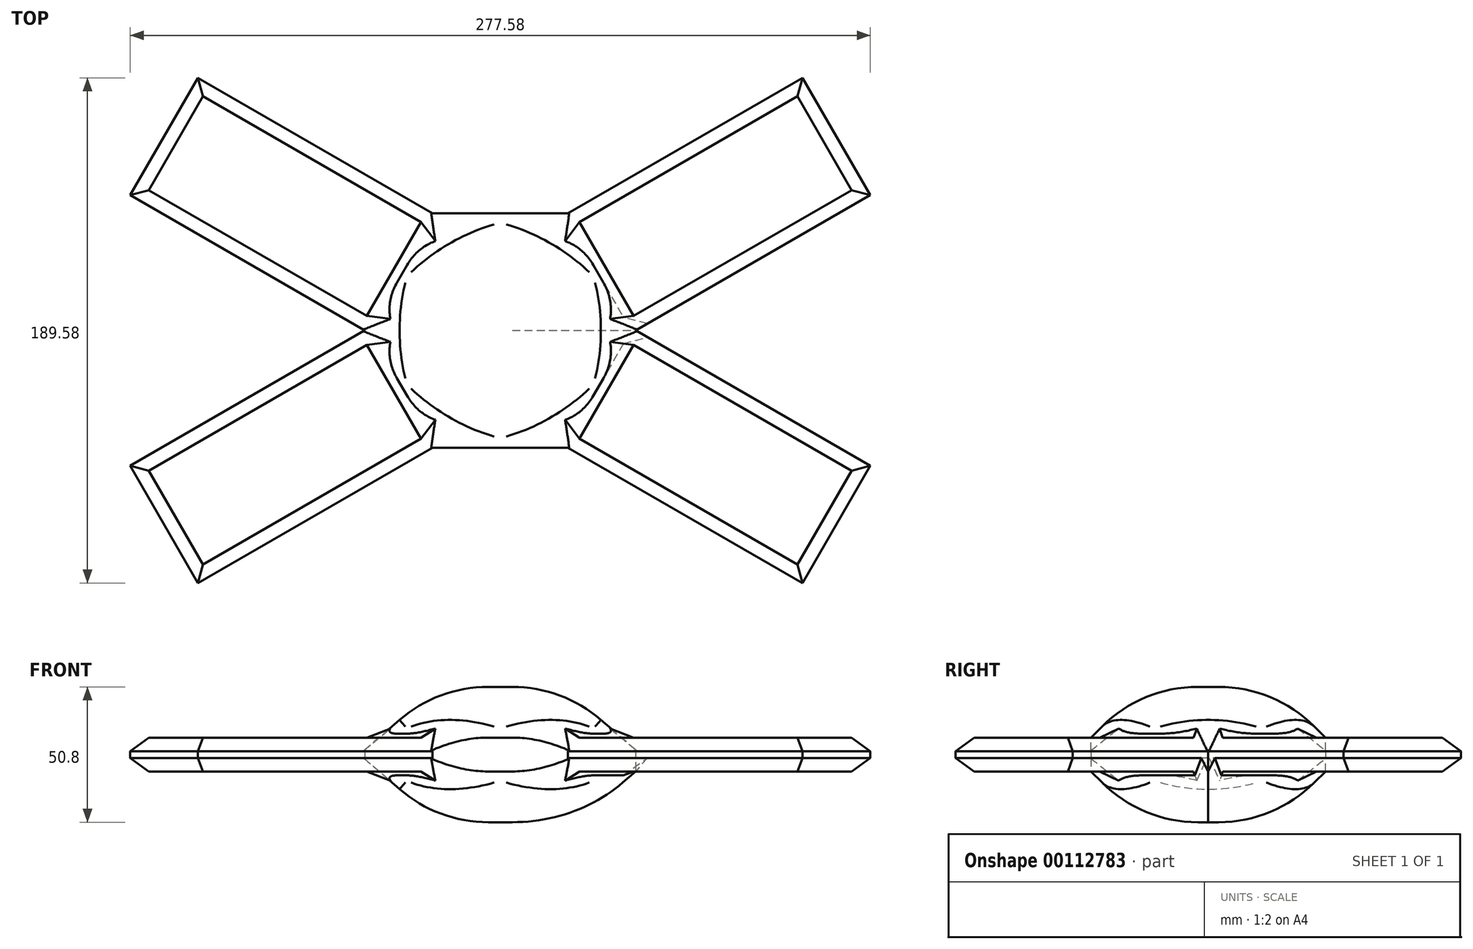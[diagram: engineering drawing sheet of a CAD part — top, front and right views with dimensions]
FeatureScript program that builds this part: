
annotation { "Feature Type Name" : "Feature", "Feature Type Description" : "" }
export const myFeature = defineFeature(function(context is Context, id is Id, definition is map)
    precondition{}
    {
        {
            var Q0;
            Q0=qCreatedBy(makeId("Top.planeOp"),FACE);
            var sketch = newSketch(context, id + "F0", { "sketchPlane" : qUnion([Q0])});
            skCircle(sketch, "E0.cCircle", {"center": v(0, 0) * mm, "radius": 44 * mm, "construction": true});
            skLineSegment(sketch, "E0.0", {"start": v(50.8, 0) * mm, "end": v(25.4, -44) * mm});
            skLineSegment(sketch, "E0.1", {"start": v(25.4, -44) * mm, "end": v(-25.4, -44) * mm});
            skLineSegment(sketch, "E0.2", {"start": v(-25.4, -44) * mm, "end": v(-50.8, 0) * mm});
            skLineSegment(sketch, "E0.3", {"start": v(-50.8, 0) * mm, "end": v(-25.4, 44) * mm});
            skLineSegment(sketch, "E0.4", {"start": v(-25.4, 44) * mm, "end": v(25.4, 44) * mm});
            skLineSegment(sketch, "E0.5", {"start": v(25.4, 44) * mm, "end": v(50.8, 0) * mm});
            skPoint(sketch, "E0.0.midPoint", {"position": v(38.1, -22) * mm});
            skLineSegment(sketch, "E1.top", {"start": v(-25.4, 145.6) * mm, "end": v(25.4, 145.6) * mm});
            skLineSegment(sketch, "E1.left", {"start": v(-25.4, 44) * mm, "end": v(-25.4, 145.6) * mm});
            skLineSegment(sketch, "E1.right", {"start": v(25.4, 44) * mm, "end": v(25.4, 145.6) * mm});
            skLineSegment(sketch, "E2.top", {"start": v(25.4, -145.6) * mm, "end": v(-25.4, -145.6) * mm});
            skLineSegment(sketch, "E2.left", {"start": v(25.4, -44) * mm, "end": v(25.4, -145.6) * mm});
            skLineSegment(sketch, "E2.right", {"start": v(-25.4, -44) * mm, "end": v(-25.4, -145.6) * mm});
            skLineSegment(sketch, "E3", {"start": v(25.4, -44) * mm, "end": v(113.39, -94.8) * mm});
            skLineSegment(sketch, "E4", {"start": v(113.39, -94.8) * mm, "end": v(138.79, -50.8) * mm});
            skLineSegment(sketch, "E5", {"start": v(138.79, -50.8) * mm, "end": v(50.8, 0) * mm});
            skLineSegment(sketch, "E6", {"start": v(-50.8, 0) * mm, "end": v(-138.79, 50.8) * mm});
            skLineSegment(sketch, "E7", {"start": v(-138.79, 50.8) * mm, "end": v(-113.39, 94.8) * mm});
            skLineSegment(sketch, "E8", {"start": v(-113.39, 94.8) * mm, "end": v(-25.4, 44) * mm});
            skLineSegment(sketch, "E9", {"start": v(-25.4, -44) * mm, "end": v(-113.39, -94.8) * mm});
            skLineSegment(sketch, "E10", {"start": v(-113.39, -94.8) * mm, "end": v(-138.79, -50.8) * mm});
            skLineSegment(sketch, "E11", {"start": v(-138.79, -50.8) * mm, "end": v(-50.8, 0) * mm});
            skLineSegment(sketch, "E12", {"start": v(50.8, 0) * mm, "end": v(138.79, 50.8) * mm});
            skLineSegment(sketch, "E13", {"start": v(138.79, 50.8) * mm, "end": v(113.39, 94.8) * mm});
            skLineSegment(sketch, "E14", {"start": v(113.39, 94.8) * mm, "end": v(25.4, 44) * mm});
            skSolve(sketch);
        }
        {
            var Q0;
            Q0=makeQuery(id+"F0.imprint","IMPRINT",FACE,{"disambiguationData":[TD([[makeQuery(id+"F0.imprint","IMPRINT",EDGE,{"derivedFrom":sQuery(id+"F0.wireOp",EDGE,"E0.5")}),1.0]])]});
            var Q1;
            Q1=makeQuery(id+"F0.imprint","IMPRINT",FACE,{"disambiguationData":[TD([[makeQuery(id+"F0.imprint","IMPRINT",EDGE,{"derivedFrom":sQuery(id+"F0.wireOp",EDGE,"E0.4")}),1.0]])]});
            var Q2;
            Q2=makeQuery(id+"F0.imprint","IMPRINT",FACE,{"disambiguationData":[TD([[makeQuery(id+"F0.imprint","IMPRINT",EDGE,{"derivedFrom":sQuery(id+"F0.wireOp",EDGE,"E0.0")}),1.0]])]});
            var Q3;
            Q3=makeQuery(id+"F0.imprint","IMPRINT",FACE,{"disambiguationData":[TD([[makeQuery(id+"F0.imprint","IMPRINT",EDGE,{"derivedFrom":sQuery(id+"F0.wireOp",EDGE,"E0.1")}),1.0]])]});
            var Q4;
            Q4=makeQuery(id+"F0.imprint","IMPRINT",FACE,{"disambiguationData":[TD([[makeQuery(id+"F0.imprint","IMPRINT",EDGE,{"derivedFrom":sQuery(id+"F0.wireOp",EDGE,"E0.2")}),1.0]])]});
            var Q5;
            Q5=makeQuery(id+"F0.imprint","IMPRINT",FACE,{"disambiguationData":[TD([[makeQuery(id+"F0.imprint","IMPRINT",EDGE,{"derivedFrom":sQuery(id+"F0.wireOp",EDGE,"E0.3")}),1.0]])]});
            var Q6;
            Q6=makeQuery(id+"F0.imprint","IMPRINT",FACE,{"disambiguationData":[TD([[makeQuery(id+"F0.imprint","IMPRINT",EDGE,{"derivedFrom":sQuery(id+"F0.wireOp",EDGE,"E0.0")}),-1.0]])]});
            extrude(context, id + "F1", {"entities" : qUnion([Q0, Q1, Q2, Q3, Q4, Q5, Q6]), "depth" : 6.35 * mm, "hasSecondDirection" : true, "secondDirectionOppositeDirection" : true, "secondDirectionDepth" : 6.35 * mm});
        }
        {
            var Q0;
            Q0=makeQuery(id+"F1.opExtrude","CAP_FACE",FACE,{"disambiguationData":[OSD([sQuery(id+"F0.wireOp",EDGE,"E1.top"),sQuery(id+"F0.wireOp",EDGE,"E1.left"),sQuery(id+"F0.wireOp",EDGE,"E1.right"),sQuery(id+"F0.wireOp",EDGE,"E2.top"),sQuery(id+"F0.wireOp",EDGE,"E2.left"),sQuery(id+"F0.wireOp",EDGE,"E2.right"),sQuery(id+"F0.wireOp",EDGE,"E3"),sQuery(id+"F0.wireOp",EDGE,"E4"),sQuery(id+"F0.wireOp",EDGE,"E5"),sQuery(id+"F0.wireOp",EDGE,"E6"),sQuery(id+"F0.wireOp",EDGE,"E7"),sQuery(id+"F0.wireOp",EDGE,"E8"),sQuery(id+"F0.wireOp",EDGE,"E9"),sQuery(id+"F0.wireOp",EDGE,"E10"),sQuery(id+"F0.wireOp",EDGE,"E11"),sQuery(id+"F0.wireOp",EDGE,"E12"),sQuery(id+"F0.wireOp",EDGE,"E13"),sQuery(id+"F0.wireOp",EDGE,"E14")])],"isStart":false});
            var sketch = newSketch(context, id + "F2", { "sketchPlane" : qUnion([Q0])});
            skLineSegment(sketch, "E15", {"start": v(-25.4, 44) * mm, "end": v(-50.8, 0) * mm});
            skLineSegment(sketch, "E16", {"start": v(-50.8, 0) * mm, "end": v(-25.4, -44) * mm});
            skLineSegment(sketch, "E17", {"start": v(-25.4, -44) * mm, "end": v(25.4, -44) * mm});
            skLineSegment(sketch, "E18", {"start": v(25.4, -44) * mm, "end": v(50.8, 0) * mm});
            skLineSegment(sketch, "E19", {"start": v(50.8, 0) * mm, "end": v(25.4, 44) * mm});
            skLineSegment(sketch, "E20", {"start": v(25.4, 44) * mm, "end": v(-25.4, 44) * mm});
            skSolve(sketch);
        }
        {
            var Q0;
            Q0=makeQuery(id+"F2.imprint","IMPRINT",FACE,{"disambiguationData":[TD([[makeQuery(id+"F2.imprint","IMPRINT",EDGE,{"derivedFrom":sQuery(id+"F2.wireOp",EDGE,"E15")}),1.0]])]});
            extrude(context, id + "F3", {"entities" : qUnion([Q0]), "operationType" : NewBodyOperationType.ADD, "depth" : 19.05 * mm});
        }
        {
            var Q0;
            Q0=makeQuery(id+"F1.opExtrude","CAP_FACE",FACE,{"disambiguationData":[OSD([sQuery(id+"F0.wireOp",EDGE,"E1.top"),sQuery(id+"F0.wireOp",EDGE,"E1.left"),sQuery(id+"F0.wireOp",EDGE,"E1.right"),sQuery(id+"F0.wireOp",EDGE,"E2.top"),sQuery(id+"F0.wireOp",EDGE,"E2.left"),sQuery(id+"F0.wireOp",EDGE,"E2.right"),sQuery(id+"F0.wireOp",EDGE,"E3"),sQuery(id+"F0.wireOp",EDGE,"E4"),sQuery(id+"F0.wireOp",EDGE,"E5"),sQuery(id+"F0.wireOp",EDGE,"E6"),sQuery(id+"F0.wireOp",EDGE,"E7"),sQuery(id+"F0.wireOp",EDGE,"E8"),sQuery(id+"F0.wireOp",EDGE,"E9"),sQuery(id+"F0.wireOp",EDGE,"E10"),sQuery(id+"F0.wireOp",EDGE,"E11"),sQuery(id+"F0.wireOp",EDGE,"E12"),sQuery(id+"F0.wireOp",EDGE,"E13"),sQuery(id+"F0.wireOp",EDGE,"E14")])],"isStart":true});
            var sketch = newSketch(context, id + "F4", { "sketchPlane" : qUnion([Q0])});
            skLineSegment(sketch, "E21", {"start": v(-25.4, 44) * mm, "end": v(-50.8, 0) * mm});
            skLineSegment(sketch, "E22", {"start": v(-50.8, 0) * mm, "end": v(-25.4, -44) * mm});
            skLineSegment(sketch, "E23", {"start": v(-25.4, -44) * mm, "end": v(25.4, -44) * mm});
            skLineSegment(sketch, "E24", {"start": v(25.4, -44) * mm, "end": v(50.8, 0) * mm});
            skLineSegment(sketch, "E25", {"start": v(50.8, 0) * mm, "end": v(25.4, 44) * mm});
            skLineSegment(sketch, "E26", {"start": v(25.4, 44) * mm, "end": v(-25.4, 44) * mm});
            skSolve(sketch);
        }
        {
            var Q0;
            Q0=makeQuery(id+"F4.imprint","IMPRINT",FACE,{"disambiguationData":[TD([[makeQuery(id+"F4.imprint","IMPRINT",EDGE,{"derivedFrom":sQuery(id+"F4.wireOp",EDGE,"E21")}),1.0]])]});
            extrude(context, id + "F5", {"entities" : qUnion([Q0]), "operationType" : NewBodyOperationType.ADD, "depth" : 19.05 * mm});
        }
        {
            var Q0;
            Q0=makeQuery(id+"F3.opExtrude","CAP_FACE",FACE,{"disambiguationData":[OSD([sQuery(id+"F2.wireOp",EDGE,"E15"),sQuery(id+"F2.wireOp",EDGE,"E16"),sQuery(id+"F2.wireOp",EDGE,"E17"),sQuery(id+"F2.wireOp",EDGE,"E18"),sQuery(id+"F2.wireOp",EDGE,"E19"),sQuery(id+"F2.wireOp",EDGE,"E20")])],"isStart":false});
            var Q1;
            Q1=makeQuery(id+"F5.opExtrude","CAP_FACE",FACE,{"disambiguationData":[OSD([sQuery(id+"F4.wireOp",EDGE,"E21"),sQuery(id+"F4.wireOp",EDGE,"E22"),sQuery(id+"F4.wireOp",EDGE,"E23"),sQuery(id+"F4.wireOp",EDGE,"E24"),sQuery(id+"F4.wireOp",EDGE,"E25"),sQuery(id+"F4.wireOp",EDGE,"E26")])],"isStart":false});
            chamfer(context, id + "F6", {"entities" : qUnion([Q0, Q1]), "width" : 19.05 * mm, "tangentPropagation" : true});
        }
        {
            var Q0;
            Q0=makeQuery(id+"F1.opExtrude","CAP_EDGE",EDGE,{"disambiguationData":[OSD([sQuery(id+"F0.wireOp",EDGE,"E5")])],"isStart":true});
            var Q1;
            Q1=makeQuery(id+"F1.opExtrude","CAP_EDGE",EDGE,{"disambiguationData":[OSD([sQuery(id+"F0.wireOp",EDGE,"E3")])],"isStart":true});
            var Q2;
            Q2=makeQuery(id+"F1.opExtrude","CAP_EDGE",EDGE,{"disambiguationData":[OSD([sQuery(id+"F0.wireOp",EDGE,"E2.left")])],"isStart":true});
            var Q3;
            Q3=makeQuery(id+"F1.opExtrude","CAP_EDGE",EDGE,{"disambiguationData":[OSD([sQuery(id+"F0.wireOp",EDGE,"E9")])],"isStart":true});
            var Q4;
            Q4=makeQuery(id+"F1.opExtrude","CAP_EDGE",EDGE,{"disambiguationData":[OSD([sQuery(id+"F0.wireOp",EDGE,"E11")])],"isStart":true});
            var Q5;
            Q5=makeQuery(id+"F1.opExtrude","CAP_EDGE",EDGE,{"disambiguationData":[OSD([sQuery(id+"F0.wireOp",EDGE,"E6")])],"isStart":true});
            var Q6;
            Q6=makeQuery(id+"F1.opExtrude","CAP_EDGE",EDGE,{"disambiguationData":[OSD([sQuery(id+"F0.wireOp",EDGE,"E8")])],"isStart":true});
            var Q7;
            Q7=makeQuery(id+"F1.opExtrude","CAP_EDGE",EDGE,{"disambiguationData":[OSD([sQuery(id+"F0.wireOp",EDGE,"E1.left")])],"isStart":true});
            var Q8;
            Q8=makeQuery(id+"F1.opExtrude","CAP_EDGE",EDGE,{"disambiguationData":[OSD([sQuery(id+"F0.wireOp",EDGE,"E1.right")])],"isStart":true});
            var Q9;
            Q9=makeQuery(id+"F1.opExtrude","CAP_EDGE",EDGE,{"disambiguationData":[OSD([sQuery(id+"F0.wireOp",EDGE,"E14")])],"isStart":true});
            var Q10;
            Q10=makeQuery(id+"F1.opExtrude","CAP_EDGE",EDGE,{"disambiguationData":[OSD([sQuery(id+"F0.wireOp",EDGE,"E12")])],"isStart":true});
            var Q11;
            Q11=makeQuery(id+"F1.opExtrude","CAP_EDGE",EDGE,{"disambiguationData":[OSD([sQuery(id+"F0.wireOp",EDGE,"E5")])],"isStart":false});
            var Q12;
            Q12=makeQuery(id+"F1.opExtrude","CAP_EDGE",EDGE,{"disambiguationData":[OSD([sQuery(id+"F0.wireOp",EDGE,"E12")])],"isStart":false});
            var Q13;
            Q13=makeQuery(id+"F1.opExtrude","CAP_EDGE",EDGE,{"disambiguationData":[OSD([sQuery(id+"F0.wireOp",EDGE,"E14")])],"isStart":false});
            var Q14;
            Q14=makeQuery(id+"F1.opExtrude","CAP_EDGE",EDGE,{"disambiguationData":[OSD([sQuery(id+"F0.wireOp",EDGE,"E1.right")])],"isStart":false});
            var Q15;
            Q15=makeQuery(id+"F1.opExtrude","CAP_EDGE",EDGE,{"disambiguationData":[OSD([sQuery(id+"F0.wireOp",EDGE,"E1.left")])],"isStart":false});
            var Q16;
            Q16=makeQuery(id+"F1.opExtrude","CAP_EDGE",EDGE,{"disambiguationData":[OSD([sQuery(id+"F0.wireOp",EDGE,"E8")])],"isStart":false});
            var Q17;
            Q17=makeQuery(id+"F1.opExtrude","CAP_EDGE",EDGE,{"disambiguationData":[OSD([sQuery(id+"F0.wireOp",EDGE,"E6")])],"isStart":false});
            var Q18;
            Q18=makeQuery(id+"F1.opExtrude","CAP_EDGE",EDGE,{"disambiguationData":[OSD([sQuery(id+"F0.wireOp",EDGE,"E11")])],"isStart":false});
            var Q19;
            Q19=makeQuery(id+"F1.opExtrude","CAP_EDGE",EDGE,{"disambiguationData":[OSD([sQuery(id+"F0.wireOp",EDGE,"E9")])],"isStart":false});
            var Q20;
            Q20=makeQuery(id+"F1.opExtrude","CAP_EDGE",EDGE,{"disambiguationData":[OSD([sQuery(id+"F0.wireOp",EDGE,"E2.right")])],"isStart":false});
            var Q21;
            Q21=makeQuery(id+"F1.opExtrude","CAP_EDGE",EDGE,{"disambiguationData":[OSD([sQuery(id+"F0.wireOp",EDGE,"E2.left")])],"isStart":false});
            var Q22;
            Q22=makeQuery(id+"F1.opExtrude","CAP_EDGE",EDGE,{"disambiguationData":[OSD([sQuery(id+"F0.wireOp",EDGE,"E3")])],"isStart":false});
            var Q23;
            Q23=makeQuery(id+"F1.opExtrude","CAP_EDGE",EDGE,{"disambiguationData":[OSD([sQuery(id+"F0.wireOp",EDGE,"E4")])],"isStart":false});
            var Q24;
            Q24=makeQuery(id+"F1.opExtrude","CAP_EDGE",EDGE,{"disambiguationData":[OSD([sQuery(id+"F0.wireOp",EDGE,"E4")])],"isStart":true});
            var Q25;
            Q25=makeQuery(id+"F1.opExtrude","CAP_EDGE",EDGE,{"disambiguationData":[OSD([sQuery(id+"F0.wireOp",EDGE,"E2.top")])],"isStart":false});
            var Q26;
            Q26=makeQuery(id+"F1.opExtrude","CAP_EDGE",EDGE,{"disambiguationData":[OSD([sQuery(id+"F0.wireOp",EDGE,"E2.top")])],"isStart":true});
            var Q27;
            Q27=makeQuery(id+"F1.opExtrude","CAP_EDGE",EDGE,{"disambiguationData":[OSD([sQuery(id+"F0.wireOp",EDGE,"E2.right")])],"isStart":true});
            var Q28;
            Q28=makeQuery(id+"F1.opExtrude","CAP_EDGE",EDGE,{"disambiguationData":[OSD([sQuery(id+"F0.wireOp",EDGE,"E10")])],"isStart":true});
            var Q29;
            Q29=makeQuery(id+"F1.opExtrude","CAP_EDGE",EDGE,{"disambiguationData":[OSD([sQuery(id+"F0.wireOp",EDGE,"E10")])],"isStart":false});
            var Q30;
            Q30=makeQuery(id+"F1.opExtrude","CAP_EDGE",EDGE,{"disambiguationData":[OSD([sQuery(id+"F0.wireOp",EDGE,"E7")])],"isStart":false});
            var Q31;
            Q31=makeQuery(id+"F1.opExtrude","CAP_EDGE",EDGE,{"disambiguationData":[OSD([sQuery(id+"F0.wireOp",EDGE,"E7")])],"isStart":true});
            var Q32;
            Q32=makeQuery(id+"F1.opExtrude","CAP_EDGE",EDGE,{"disambiguationData":[OSD([sQuery(id+"F0.wireOp",EDGE,"E1.top")])],"isStart":true});
            var Q33;
            Q33=makeQuery(id+"F1.opExtrude","CAP_EDGE",EDGE,{"disambiguationData":[OSD([sQuery(id+"F0.wireOp",EDGE,"E1.top")])],"isStart":false});
            var Q34;
            Q34=makeQuery(id+"F1.opExtrude","CAP_EDGE",EDGE,{"disambiguationData":[OSD([sQuery(id+"F0.wireOp",EDGE,"E13")])],"isStart":true});
            var Q35;
            Q35=makeQuery(id+"F1.opExtrude","CAP_EDGE",EDGE,{"disambiguationData":[OSD([sQuery(id+"F0.wireOp",EDGE,"E13")])],"isStart":false});
            chamfer(context, id + "F7", {"entities" : qUnion([Q0, Q1, Q2, Q3, Q4, Q5, Q6, Q7, Q8, Q9, Q10, Q11, Q12, Q13, Q14, Q15, Q16, Q17, Q18, Q19, Q20, Q21, Q22, Q23, Q24, Q25, Q26, Q27, Q28, Q29, Q30, Q31, Q32, Q33, Q34, Q35]), "width" : 5.08 * mm, "tangentPropagation" : true});
        }
        {
            var Q0;
            {var subQ0=sQuery(id+"F0.wireOp",EDGE,"E9");var subQ1=sQuery(id+"F0.wireOp",EDGE,"E2.right");var subQ2=sQuery(id+"F2.wireOp",EDGE,"E16");var subQ3=sQuery(id+"F0.wireOp",EDGE,"E6");var subQ4=sQuery(id+"F0.wireOp",EDGE,"E11");var subQ5=sQuery(id+"F0.wireOp",EDGE,"E10");var subQ6=makeQuery(id+"F1.opExtrude","CAP_FACE",FACE,{"disambiguationData":[OSD([sQuery(id+"F0.wireOp",EDGE,"E1.top"),sQuery(id+"F0.wireOp",EDGE,"E1.left"),sQuery(id+"F0.wireOp",EDGE,"E1.right"),sQuery(id+"F0.wireOp",EDGE,"E2.top"),sQuery(id+"F0.wireOp",EDGE,"E2.left"),subQ1,sQuery(id+"F0.wireOp",EDGE,"E3"),sQuery(id+"F0.wireOp",EDGE,"E4"),sQuery(id+"F0.wireOp",EDGE,"E5"),subQ3,sQuery(id+"F0.wireOp",EDGE,"E7"),sQuery(id+"F0.wireOp",EDGE,"E8"),subQ0,subQ5,subQ4,sQuery(id+"F0.wireOp",EDGE,"E12"),sQuery(id+"F0.wireOp",EDGE,"E13"),sQuery(id+"F0.wireOp",EDGE,"E14")])],"isStart":false});Q0=makeQuery(id+"F6.opChamfer","BLEND_EDGE",EDGE,{"blendedFrom":[makeQuery(id+"F3.opExtrude","CAP_EDGE",EDGE,{"disambiguationData":[OSD([subQ2])],"isStart":false}),makeQuery(id+"F3.boolean.opBoolean","SPLIT",FACE,{"disambiguationData":[TD([makeQuery(id+"F1.opExtrude","SWEPT_FACE",FACE,{"disambiguationData":[OSD([subQ5])]})])],"derivedFrom":subQ6})],"blendedInto":[makeQuery(id+"F3.boolean.opBoolean","SPLIT",FACE,{"disambiguationData":[TD([makeQuery(id+"F1.opExtrude","SWEPT_FACE",FACE,{"disambiguationData":[OSD([subQ5])]})])],"derivedFrom":subQ6})]});}
            var Q1;
            {var subQ0=sQuery(id+"F0.wireOp",EDGE,"E2.right");var subQ1=sQuery(id+"F0.wireOp",EDGE,"E9");var subQ2=sQuery(id+"F0.wireOp",EDGE,"E2.left");var subQ3=sQuery(id+"F0.wireOp",EDGE,"E2.top");var subQ4=sQuery(id+"F0.wireOp",EDGE,"E3");var subQ5=makeQuery(id+"F1.opExtrude","CAP_FACE",FACE,{"disambiguationData":[OSD([sQuery(id+"F0.wireOp",EDGE,"E1.top"),sQuery(id+"F0.wireOp",EDGE,"E1.left"),sQuery(id+"F0.wireOp",EDGE,"E1.right"),subQ3,subQ2,subQ0,subQ4,sQuery(id+"F0.wireOp",EDGE,"E4"),sQuery(id+"F0.wireOp",EDGE,"E5"),sQuery(id+"F0.wireOp",EDGE,"E6"),sQuery(id+"F0.wireOp",EDGE,"E7"),sQuery(id+"F0.wireOp",EDGE,"E8"),subQ1,sQuery(id+"F0.wireOp",EDGE,"E10"),sQuery(id+"F0.wireOp",EDGE,"E11"),sQuery(id+"F0.wireOp",EDGE,"E12"),sQuery(id+"F0.wireOp",EDGE,"E13"),sQuery(id+"F0.wireOp",EDGE,"E14")])],"isStart":false});var subQ6=sQuery(id+"F2.wireOp",EDGE,"E17");Q1=makeQuery(id+"F6.opChamfer","BLEND_EDGE",EDGE,{"blendedFrom":[makeQuery(id+"F3.opExtrude","CAP_EDGE",EDGE,{"disambiguationData":[OSD([subQ6])],"isStart":false}),makeQuery(id+"F3.boolean.opBoolean","SPLIT",FACE,{"disambiguationData":[TD([makeQuery(id+"F1.opExtrude","SWEPT_FACE",FACE,{"disambiguationData":[OSD([subQ3])]})])],"derivedFrom":subQ5})],"blendedInto":[makeQuery(id+"F3.boolean.opBoolean","SPLIT",FACE,{"disambiguationData":[TD([makeQuery(id+"F1.opExtrude","SWEPT_FACE",FACE,{"disambiguationData":[OSD([subQ3])]})])],"derivedFrom":subQ5})]});}
            var Q2;
            {var subQ0=sQuery(id+"F0.wireOp",EDGE,"E2.left");var subQ1=sQuery(id+"F0.wireOp",EDGE,"E4");var subQ2=sQuery(id+"F0.wireOp",EDGE,"E12");var subQ3=sQuery(id+"F0.wireOp",EDGE,"E3");var subQ4=sQuery(id+"F2.wireOp",EDGE,"E18");var subQ5=sQuery(id+"F0.wireOp",EDGE,"E5");var subQ6=makeQuery(id+"F1.opExtrude","CAP_FACE",FACE,{"disambiguationData":[OSD([sQuery(id+"F0.wireOp",EDGE,"E1.top"),sQuery(id+"F0.wireOp",EDGE,"E1.left"),sQuery(id+"F0.wireOp",EDGE,"E1.right"),sQuery(id+"F0.wireOp",EDGE,"E2.top"),subQ0,sQuery(id+"F0.wireOp",EDGE,"E2.right"),subQ3,subQ1,subQ5,sQuery(id+"F0.wireOp",EDGE,"E6"),sQuery(id+"F0.wireOp",EDGE,"E7"),sQuery(id+"F0.wireOp",EDGE,"E8"),sQuery(id+"F0.wireOp",EDGE,"E9"),sQuery(id+"F0.wireOp",EDGE,"E10"),sQuery(id+"F0.wireOp",EDGE,"E11"),subQ2,sQuery(id+"F0.wireOp",EDGE,"E13"),sQuery(id+"F0.wireOp",EDGE,"E14")])],"isStart":false});Q2=makeQuery(id+"F6.opChamfer","BLEND_EDGE",EDGE,{"blendedFrom":[makeQuery(id+"F3.opExtrude","CAP_EDGE",EDGE,{"disambiguationData":[OSD([subQ4])],"isStart":false}),makeQuery(id+"F3.boolean.opBoolean","SPLIT",FACE,{"disambiguationData":[TD([makeQuery(id+"F1.opExtrude","SWEPT_FACE",FACE,{"disambiguationData":[OSD([subQ1])]})])],"derivedFrom":subQ6})],"blendedInto":[makeQuery(id+"F3.boolean.opBoolean","SPLIT",FACE,{"disambiguationData":[TD([makeQuery(id+"F1.opExtrude","SWEPT_FACE",FACE,{"disambiguationData":[OSD([subQ1])]})])],"derivedFrom":subQ6})]});}
            var Q3;
            {var subQ0=sQuery(id+"F0.wireOp",EDGE,"E7");var subQ1=sQuery(id+"F2.wireOp",EDGE,"E15");var subQ2=sQuery(id+"F0.wireOp",EDGE,"E6");var subQ3=sQuery(id+"F0.wireOp",EDGE,"E1.left");var subQ4=sQuery(id+"F0.wireOp",EDGE,"E11");var subQ5=sQuery(id+"F0.wireOp",EDGE,"E8");var subQ6=makeQuery(id+"F1.opExtrude","CAP_FACE",FACE,{"disambiguationData":[OSD([sQuery(id+"F0.wireOp",EDGE,"E1.top"),subQ3,sQuery(id+"F0.wireOp",EDGE,"E1.right"),sQuery(id+"F0.wireOp",EDGE,"E2.top"),sQuery(id+"F0.wireOp",EDGE,"E2.left"),sQuery(id+"F0.wireOp",EDGE,"E2.right"),sQuery(id+"F0.wireOp",EDGE,"E3"),sQuery(id+"F0.wireOp",EDGE,"E4"),sQuery(id+"F0.wireOp",EDGE,"E5"),subQ2,subQ0,subQ5,sQuery(id+"F0.wireOp",EDGE,"E9"),sQuery(id+"F0.wireOp",EDGE,"E10"),subQ4,sQuery(id+"F0.wireOp",EDGE,"E12"),sQuery(id+"F0.wireOp",EDGE,"E13"),sQuery(id+"F0.wireOp",EDGE,"E14")])],"isStart":false});Q3=makeQuery(id+"F6.opChamfer","BLEND_EDGE",EDGE,{"blendedFrom":[makeQuery(id+"F3.opExtrude","CAP_EDGE",EDGE,{"disambiguationData":[OSD([subQ1])],"isStart":false}),makeQuery(id+"F3.boolean.opBoolean","SPLIT",FACE,{"disambiguationData":[TD([makeQuery(id+"F1.opExtrude","SWEPT_FACE",FACE,{"disambiguationData":[OSD([subQ0])]})])],"derivedFrom":subQ6})],"blendedInto":[makeQuery(id+"F3.boolean.opBoolean","SPLIT",FACE,{"disambiguationData":[TD([makeQuery(id+"F1.opExtrude","SWEPT_FACE",FACE,{"disambiguationData":[OSD([subQ0])]})])],"derivedFrom":subQ6})]});}
            var Q4;
            {var subQ0=sQuery(id+"F0.wireOp",EDGE,"E1.right");var subQ1=sQuery(id+"F0.wireOp",EDGE,"E1.left");var subQ2=sQuery(id+"F0.wireOp",EDGE,"E14");var subQ3=sQuery(id+"F0.wireOp",EDGE,"E8");var subQ4=sQuery(id+"F0.wireOp",EDGE,"E1.top");var subQ5=makeQuery(id+"F1.opExtrude","CAP_FACE",FACE,{"disambiguationData":[OSD([subQ4,subQ1,subQ0,sQuery(id+"F0.wireOp",EDGE,"E2.top"),sQuery(id+"F0.wireOp",EDGE,"E2.left"),sQuery(id+"F0.wireOp",EDGE,"E2.right"),sQuery(id+"F0.wireOp",EDGE,"E3"),sQuery(id+"F0.wireOp",EDGE,"E4"),sQuery(id+"F0.wireOp",EDGE,"E5"),sQuery(id+"F0.wireOp",EDGE,"E6"),sQuery(id+"F0.wireOp",EDGE,"E7"),subQ3,sQuery(id+"F0.wireOp",EDGE,"E9"),sQuery(id+"F0.wireOp",EDGE,"E10"),sQuery(id+"F0.wireOp",EDGE,"E11"),sQuery(id+"F0.wireOp",EDGE,"E12"),sQuery(id+"F0.wireOp",EDGE,"E13"),subQ2])],"isStart":false});var subQ6=sQuery(id+"F2.wireOp",EDGE,"E20");Q4=makeQuery(id+"F6.opChamfer","BLEND_EDGE",EDGE,{"blendedFrom":[makeQuery(id+"F3.opExtrude","CAP_EDGE",EDGE,{"disambiguationData":[OSD([subQ6])],"isStart":false}),makeQuery(id+"F3.boolean.opBoolean","SPLIT",FACE,{"disambiguationData":[TD([makeQuery(id+"F1.opExtrude","SWEPT_FACE",FACE,{"disambiguationData":[OSD([subQ4])]})])],"derivedFrom":subQ5})],"blendedInto":[makeQuery(id+"F3.boolean.opBoolean","SPLIT",FACE,{"disambiguationData":[TD([makeQuery(id+"F1.opExtrude","SWEPT_FACE",FACE,{"disambiguationData":[OSD([subQ4])]})])],"derivedFrom":subQ5})]});}
            var Q5;
            {var subQ0=sQuery(id+"F0.wireOp",EDGE,"E5");var subQ1=sQuery(id+"F0.wireOp",EDGE,"E14");var subQ2=sQuery(id+"F0.wireOp",EDGE,"E1.right");var subQ3=sQuery(id+"F0.wireOp",EDGE,"E12");var subQ4=sQuery(id+"F0.wireOp",EDGE,"E13");var subQ5=makeQuery(id+"F1.opExtrude","CAP_FACE",FACE,{"disambiguationData":[OSD([sQuery(id+"F0.wireOp",EDGE,"E1.top"),sQuery(id+"F0.wireOp",EDGE,"E1.left"),subQ2,sQuery(id+"F0.wireOp",EDGE,"E2.top"),sQuery(id+"F0.wireOp",EDGE,"E2.left"),sQuery(id+"F0.wireOp",EDGE,"E2.right"),sQuery(id+"F0.wireOp",EDGE,"E3"),sQuery(id+"F0.wireOp",EDGE,"E4"),subQ0,sQuery(id+"F0.wireOp",EDGE,"E6"),sQuery(id+"F0.wireOp",EDGE,"E7"),sQuery(id+"F0.wireOp",EDGE,"E8"),sQuery(id+"F0.wireOp",EDGE,"E9"),sQuery(id+"F0.wireOp",EDGE,"E10"),sQuery(id+"F0.wireOp",EDGE,"E11"),subQ3,subQ4,subQ1])],"isStart":false});var subQ6=sQuery(id+"F2.wireOp",EDGE,"E19");Q5=makeQuery(id+"F6.opChamfer","BLEND_EDGE",EDGE,{"blendedFrom":[makeQuery(id+"F3.opExtrude","CAP_EDGE",EDGE,{"disambiguationData":[OSD([subQ6])],"isStart":false}),makeQuery(id+"F3.boolean.opBoolean","SPLIT",FACE,{"disambiguationData":[TD([makeQuery(id+"F1.opExtrude","SWEPT_FACE",FACE,{"disambiguationData":[OSD([subQ4])]})])],"derivedFrom":subQ5})],"blendedInto":[makeQuery(id+"F3.boolean.opBoolean","SPLIT",FACE,{"disambiguationData":[TD([makeQuery(id+"F1.opExtrude","SWEPT_FACE",FACE,{"disambiguationData":[OSD([subQ4])]})])],"derivedFrom":subQ5})]});}
            var Q6;
            {var subQ0=sQuery(id+"F0.wireOp",EDGE,"E4");var subQ1=sQuery(id+"F0.wireOp",EDGE,"E12");var subQ2=sQuery(id+"F0.wireOp",EDGE,"E3");var subQ3=sQuery(id+"F0.wireOp",EDGE,"E5");var subQ4=sQuery(id+"F0.wireOp",EDGE,"E2.left");var subQ5=makeQuery(id+"F1.opExtrude","CAP_FACE",FACE,{"disambiguationData":[OSD([sQuery(id+"F0.wireOp",EDGE,"E1.top"),sQuery(id+"F0.wireOp",EDGE,"E1.left"),sQuery(id+"F0.wireOp",EDGE,"E1.right"),sQuery(id+"F0.wireOp",EDGE,"E2.top"),subQ4,sQuery(id+"F0.wireOp",EDGE,"E2.right"),subQ2,subQ0,subQ3,sQuery(id+"F0.wireOp",EDGE,"E6"),sQuery(id+"F0.wireOp",EDGE,"E7"),sQuery(id+"F0.wireOp",EDGE,"E8"),sQuery(id+"F0.wireOp",EDGE,"E9"),sQuery(id+"F0.wireOp",EDGE,"E10"),sQuery(id+"F0.wireOp",EDGE,"E11"),subQ1,sQuery(id+"F0.wireOp",EDGE,"E13"),sQuery(id+"F0.wireOp",EDGE,"E14")])],"isStart":true});var subQ6=sQuery(id+"F4.wireOp",EDGE,"E25");Q6=makeQuery(id+"F6.opChamfer","BLEND_EDGE",EDGE,{"blendedFrom":[makeQuery(id+"F5.opExtrude","CAP_EDGE",EDGE,{"disambiguationData":[OSD([subQ6])],"isStart":false}),makeQuery(id+"F5.boolean.opBoolean","SPLIT",FACE,{"disambiguationData":[TD([makeQuery(id+"F1.opExtrude","SWEPT_FACE",FACE,{"disambiguationData":[OSD([subQ0])]})])],"derivedFrom":subQ5})],"blendedInto":[makeQuery(id+"F5.boolean.opBoolean","SPLIT",FACE,{"disambiguationData":[TD([makeQuery(id+"F1.opExtrude","SWEPT_FACE",FACE,{"disambiguationData":[OSD([subQ0])]})])],"derivedFrom":subQ5})]});}
            var Q7;
            {var subQ0=sQuery(id+"F0.wireOp",EDGE,"E2.right");var subQ1=sQuery(id+"F0.wireOp",EDGE,"E9");var subQ2=sQuery(id+"F0.wireOp",EDGE,"E2.left");var subQ3=sQuery(id+"F0.wireOp",EDGE,"E2.top");var subQ4=sQuery(id+"F0.wireOp",EDGE,"E3");var subQ5=makeQuery(id+"F1.opExtrude","CAP_FACE",FACE,{"disambiguationData":[OSD([sQuery(id+"F0.wireOp",EDGE,"E1.top"),sQuery(id+"F0.wireOp",EDGE,"E1.left"),sQuery(id+"F0.wireOp",EDGE,"E1.right"),subQ3,subQ2,subQ0,subQ4,sQuery(id+"F0.wireOp",EDGE,"E4"),sQuery(id+"F0.wireOp",EDGE,"E5"),sQuery(id+"F0.wireOp",EDGE,"E6"),sQuery(id+"F0.wireOp",EDGE,"E7"),sQuery(id+"F0.wireOp",EDGE,"E8"),subQ1,sQuery(id+"F0.wireOp",EDGE,"E10"),sQuery(id+"F0.wireOp",EDGE,"E11"),sQuery(id+"F0.wireOp",EDGE,"E12"),sQuery(id+"F0.wireOp",EDGE,"E13"),sQuery(id+"F0.wireOp",EDGE,"E14")])],"isStart":true});var subQ6=sQuery(id+"F4.wireOp",EDGE,"E26");Q7=makeQuery(id+"F6.opChamfer","BLEND_EDGE",EDGE,{"blendedFrom":[makeQuery(id+"F5.opExtrude","CAP_EDGE",EDGE,{"disambiguationData":[OSD([subQ6])],"isStart":false}),makeQuery(id+"F5.boolean.opBoolean","SPLIT",FACE,{"disambiguationData":[TD([makeQuery(id+"F1.opExtrude","SWEPT_FACE",FACE,{"disambiguationData":[OSD([subQ3])]})])],"derivedFrom":subQ5})],"blendedInto":[makeQuery(id+"F5.boolean.opBoolean","SPLIT",FACE,{"disambiguationData":[TD([makeQuery(id+"F1.opExtrude","SWEPT_FACE",FACE,{"disambiguationData":[OSD([subQ3])]})])],"derivedFrom":subQ5})]});}
            var Q8;
            {var subQ0=sQuery(id+"F0.wireOp",EDGE,"E6");var subQ1=sQuery(id+"F0.wireOp",EDGE,"E2.right");var subQ2=sQuery(id+"F0.wireOp",EDGE,"E9");var subQ3=sQuery(id+"F0.wireOp",EDGE,"E11");var subQ4=sQuery(id+"F0.wireOp",EDGE,"E10");var subQ5=makeQuery(id+"F1.opExtrude","CAP_FACE",FACE,{"disambiguationData":[OSD([sQuery(id+"F0.wireOp",EDGE,"E1.top"),sQuery(id+"F0.wireOp",EDGE,"E1.left"),sQuery(id+"F0.wireOp",EDGE,"E1.right"),sQuery(id+"F0.wireOp",EDGE,"E2.top"),sQuery(id+"F0.wireOp",EDGE,"E2.left"),subQ1,sQuery(id+"F0.wireOp",EDGE,"E3"),sQuery(id+"F0.wireOp",EDGE,"E4"),sQuery(id+"F0.wireOp",EDGE,"E5"),subQ0,sQuery(id+"F0.wireOp",EDGE,"E7"),sQuery(id+"F0.wireOp",EDGE,"E8"),subQ2,subQ4,subQ3,sQuery(id+"F0.wireOp",EDGE,"E12"),sQuery(id+"F0.wireOp",EDGE,"E13"),sQuery(id+"F0.wireOp",EDGE,"E14")])],"isStart":true});var subQ6=sQuery(id+"F4.wireOp",EDGE,"E21");Q8=makeQuery(id+"F6.opChamfer","BLEND_EDGE",EDGE,{"blendedFrom":[makeQuery(id+"F5.opExtrude","CAP_EDGE",EDGE,{"disambiguationData":[OSD([subQ6])],"isStart":false}),makeQuery(id+"F5.boolean.opBoolean","SPLIT",FACE,{"disambiguationData":[TD([makeQuery(id+"F1.opExtrude","SWEPT_FACE",FACE,{"disambiguationData":[OSD([subQ4])]})])],"derivedFrom":subQ5})],"blendedInto":[makeQuery(id+"F5.boolean.opBoolean","SPLIT",FACE,{"disambiguationData":[TD([makeQuery(id+"F1.opExtrude","SWEPT_FACE",FACE,{"disambiguationData":[OSD([subQ4])]})])],"derivedFrom":subQ5})]});}
            var Q9;
            {var subQ0=sQuery(id+"F0.wireOp",EDGE,"E12");var subQ1=sQuery(id+"F0.wireOp",EDGE,"E5");var subQ2=sQuery(id+"F0.wireOp",EDGE,"E14");var subQ3=sQuery(id+"F0.wireOp",EDGE,"E1.right");var subQ4=sQuery(id+"F4.wireOp",EDGE,"E24");var subQ5=sQuery(id+"F0.wireOp",EDGE,"E13");var subQ6=makeQuery(id+"F1.opExtrude","CAP_FACE",FACE,{"disambiguationData":[OSD([sQuery(id+"F0.wireOp",EDGE,"E1.top"),sQuery(id+"F0.wireOp",EDGE,"E1.left"),subQ3,sQuery(id+"F0.wireOp",EDGE,"E2.top"),sQuery(id+"F0.wireOp",EDGE,"E2.left"),sQuery(id+"F0.wireOp",EDGE,"E2.right"),sQuery(id+"F0.wireOp",EDGE,"E3"),sQuery(id+"F0.wireOp",EDGE,"E4"),subQ1,sQuery(id+"F0.wireOp",EDGE,"E6"),sQuery(id+"F0.wireOp",EDGE,"E7"),sQuery(id+"F0.wireOp",EDGE,"E8"),sQuery(id+"F0.wireOp",EDGE,"E9"),sQuery(id+"F0.wireOp",EDGE,"E10"),sQuery(id+"F0.wireOp",EDGE,"E11"),subQ0,subQ5,subQ2])],"isStart":true});Q9=makeQuery(id+"F6.opChamfer","BLEND_EDGE",EDGE,{"blendedFrom":[makeQuery(id+"F5.opExtrude","CAP_EDGE",EDGE,{"disambiguationData":[OSD([subQ4])],"isStart":false}),makeQuery(id+"F5.boolean.opBoolean","SPLIT",FACE,{"disambiguationData":[TD([makeQuery(id+"F1.opExtrude","SWEPT_FACE",FACE,{"disambiguationData":[OSD([subQ5])]})])],"derivedFrom":subQ6})],"blendedInto":[makeQuery(id+"F5.boolean.opBoolean","SPLIT",FACE,{"disambiguationData":[TD([makeQuery(id+"F1.opExtrude","SWEPT_FACE",FACE,{"disambiguationData":[OSD([subQ5])]})])],"derivedFrom":subQ6})]});}
            var Q10;
            {var subQ0=sQuery(id+"F0.wireOp",EDGE,"E7");var subQ1=sQuery(id+"F0.wireOp",EDGE,"E6");var subQ2=sQuery(id+"F0.wireOp",EDGE,"E1.left");var subQ3=sQuery(id+"F0.wireOp",EDGE,"E11");var subQ4=sQuery(id+"F0.wireOp",EDGE,"E8");var subQ5=makeQuery(id+"F1.opExtrude","CAP_FACE",FACE,{"disambiguationData":[OSD([sQuery(id+"F0.wireOp",EDGE,"E1.top"),subQ2,sQuery(id+"F0.wireOp",EDGE,"E1.right"),sQuery(id+"F0.wireOp",EDGE,"E2.top"),sQuery(id+"F0.wireOp",EDGE,"E2.left"),sQuery(id+"F0.wireOp",EDGE,"E2.right"),sQuery(id+"F0.wireOp",EDGE,"E3"),sQuery(id+"F0.wireOp",EDGE,"E4"),sQuery(id+"F0.wireOp",EDGE,"E5"),subQ1,subQ0,subQ4,sQuery(id+"F0.wireOp",EDGE,"E9"),sQuery(id+"F0.wireOp",EDGE,"E10"),subQ3,sQuery(id+"F0.wireOp",EDGE,"E12"),sQuery(id+"F0.wireOp",EDGE,"E13"),sQuery(id+"F0.wireOp",EDGE,"E14")])],"isStart":true});var subQ6=sQuery(id+"F4.wireOp",EDGE,"E22");Q10=makeQuery(id+"F6.opChamfer","BLEND_EDGE",EDGE,{"blendedFrom":[makeQuery(id+"F5.opExtrude","CAP_EDGE",EDGE,{"disambiguationData":[OSD([subQ6])],"isStart":false}),makeQuery(id+"F5.boolean.opBoolean","SPLIT",FACE,{"disambiguationData":[TD([makeQuery(id+"F1.opExtrude","SWEPT_FACE",FACE,{"disambiguationData":[OSD([subQ0])]})])],"derivedFrom":subQ5})],"blendedInto":[makeQuery(id+"F5.boolean.opBoolean","SPLIT",FACE,{"disambiguationData":[TD([makeQuery(id+"F1.opExtrude","SWEPT_FACE",FACE,{"disambiguationData":[OSD([subQ0])]})])],"derivedFrom":subQ5})]});}
            chamfer(context, id + "F8", {"entities" : qUnion([Q0, Q1, Q2, Q3, Q4, Q5, Q6, Q7, Q8, Q9, Q10]), "width" : 5.08 * mm, "tangentPropagation" : true});
        }
        {
            var Q0;
            {var subQ0=sQuery(id+"F2.wireOp",EDGE,"E17");Q0=makeQuery(id+"F6.opChamfer","BLEND_EDGE",EDGE,{"blendedFrom":[makeQuery(id+"F3.opExtrude","CAP_EDGE",EDGE,{"disambiguationData":[OSD([subQ0])],"isStart":false}),makeQuery(id+"F3.opExtrude","CAP_FACE",FACE,{"disambiguationData":[OSD([sQuery(id+"F2.wireOp",EDGE,"E15"),sQuery(id+"F2.wireOp",EDGE,"E16"),subQ0,sQuery(id+"F2.wireOp",EDGE,"E18"),sQuery(id+"F2.wireOp",EDGE,"E19"),sQuery(id+"F2.wireOp",EDGE,"E20")])],"isStart":false})],"blendedInto":[makeQuery(id+"F3.opExtrude","CAP_FACE",FACE,{"disambiguationData":[OSD([sQuery(id+"F2.wireOp",EDGE,"E15"),sQuery(id+"F2.wireOp",EDGE,"E16"),subQ0,sQuery(id+"F2.wireOp",EDGE,"E18"),sQuery(id+"F2.wireOp",EDGE,"E19"),sQuery(id+"F2.wireOp",EDGE,"E20")])],"isStart":false})]});}
            var Q1;
            {var subQ0=sQuery(id+"F2.wireOp",EDGE,"E16");Q1=makeQuery(id+"F6.opChamfer","BLEND_EDGE",EDGE,{"blendedFrom":[makeQuery(id+"F3.opExtrude","CAP_EDGE",EDGE,{"disambiguationData":[OSD([subQ0])],"isStart":false}),makeQuery(id+"F3.opExtrude","CAP_FACE",FACE,{"disambiguationData":[OSD([sQuery(id+"F2.wireOp",EDGE,"E15"),subQ0,sQuery(id+"F2.wireOp",EDGE,"E17"),sQuery(id+"F2.wireOp",EDGE,"E18"),sQuery(id+"F2.wireOp",EDGE,"E19"),sQuery(id+"F2.wireOp",EDGE,"E20")])],"isStart":false})],"blendedInto":[makeQuery(id+"F3.opExtrude","CAP_FACE",FACE,{"disambiguationData":[OSD([sQuery(id+"F2.wireOp",EDGE,"E15"),subQ0,sQuery(id+"F2.wireOp",EDGE,"E17"),sQuery(id+"F2.wireOp",EDGE,"E18"),sQuery(id+"F2.wireOp",EDGE,"E19"),sQuery(id+"F2.wireOp",EDGE,"E20")])],"isStart":false})]});}
            var Q2;
            Q2=makeQuery(id+"F6.opChamfer","BLEND_EDGE",EDGE,{"blendedFrom":[makeQuery(id+"F3.opExtrude","CAP_EDGE",EDGE,{"disambiguationData":[OSD([sQuery(id+"F2.wireOp",EDGE,"E16")])],"isStart":false}),makeQuery(id+"F3.opExtrude","CAP_EDGE",EDGE,{"disambiguationData":[OSD([sQuery(id+"F2.wireOp",EDGE,"E17")])],"isStart":false})],"blendedInto":[]});
            var Q3;
            Q3=makeQuery(id+"F6.opChamfer","BLEND_EDGE",EDGE,{"blendedFrom":[makeQuery(id+"F3.opExtrude","CAP_EDGE",EDGE,{"disambiguationData":[OSD([sQuery(id+"F2.wireOp",EDGE,"E17")])],"isStart":false}),makeQuery(id+"F3.opExtrude","CAP_EDGE",EDGE,{"disambiguationData":[OSD([sQuery(id+"F2.wireOp",EDGE,"E18")])],"isStart":false})],"blendedInto":[]});
            var Q4;
            {var subQ0=sQuery(id+"F2.wireOp",EDGE,"E18");Q4=makeQuery(id+"F6.opChamfer","BLEND_EDGE",EDGE,{"blendedFrom":[makeQuery(id+"F3.opExtrude","CAP_EDGE",EDGE,{"disambiguationData":[OSD([subQ0])],"isStart":false}),makeQuery(id+"F3.opExtrude","CAP_FACE",FACE,{"disambiguationData":[OSD([sQuery(id+"F2.wireOp",EDGE,"E15"),sQuery(id+"F2.wireOp",EDGE,"E16"),sQuery(id+"F2.wireOp",EDGE,"E17"),subQ0,sQuery(id+"F2.wireOp",EDGE,"E19"),sQuery(id+"F2.wireOp",EDGE,"E20")])],"isStart":false})],"blendedInto":[makeQuery(id+"F3.opExtrude","CAP_FACE",FACE,{"disambiguationData":[OSD([sQuery(id+"F2.wireOp",EDGE,"E15"),sQuery(id+"F2.wireOp",EDGE,"E16"),sQuery(id+"F2.wireOp",EDGE,"E17"),subQ0,sQuery(id+"F2.wireOp",EDGE,"E19"),sQuery(id+"F2.wireOp",EDGE,"E20")])],"isStart":false})]});}
            var Q5;
            {var subQ0=sQuery(id+"F2.wireOp",EDGE,"E19");Q5=makeQuery(id+"F6.opChamfer","BLEND_EDGE",EDGE,{"blendedFrom":[makeQuery(id+"F3.opExtrude","CAP_EDGE",EDGE,{"disambiguationData":[OSD([subQ0])],"isStart":false}),makeQuery(id+"F3.opExtrude","CAP_FACE",FACE,{"disambiguationData":[OSD([sQuery(id+"F2.wireOp",EDGE,"E15"),sQuery(id+"F2.wireOp",EDGE,"E16"),sQuery(id+"F2.wireOp",EDGE,"E17"),sQuery(id+"F2.wireOp",EDGE,"E18"),subQ0,sQuery(id+"F2.wireOp",EDGE,"E20")])],"isStart":false})],"blendedInto":[makeQuery(id+"F3.opExtrude","CAP_FACE",FACE,{"disambiguationData":[OSD([sQuery(id+"F2.wireOp",EDGE,"E15"),sQuery(id+"F2.wireOp",EDGE,"E16"),sQuery(id+"F2.wireOp",EDGE,"E17"),sQuery(id+"F2.wireOp",EDGE,"E18"),subQ0,sQuery(id+"F2.wireOp",EDGE,"E20")])],"isStart":false})]});}
            var Q6;
            Q6=makeQuery(id+"F6.opChamfer","BLEND_EDGE",EDGE,{"blendedFrom":[makeQuery(id+"F3.opExtrude","CAP_EDGE",EDGE,{"disambiguationData":[OSD([sQuery(id+"F2.wireOp",EDGE,"E18")])],"isStart":false}),makeQuery(id+"F3.opExtrude","CAP_EDGE",EDGE,{"disambiguationData":[OSD([sQuery(id+"F2.wireOp",EDGE,"E19")])],"isStart":false})],"blendedInto":[]});
            var Q7;
            Q7=makeQuery(id+"F6.opChamfer","BLEND_EDGE",EDGE,{"blendedFrom":[makeQuery(id+"F3.opExtrude","CAP_EDGE",EDGE,{"disambiguationData":[OSD([sQuery(id+"F2.wireOp",EDGE,"E19")])],"isStart":false}),makeQuery(id+"F3.opExtrude","CAP_EDGE",EDGE,{"disambiguationData":[OSD([sQuery(id+"F2.wireOp",EDGE,"E20")])],"isStart":false})],"blendedInto":[]});
            var Q8;
            {var subQ0=sQuery(id+"F2.wireOp",EDGE,"E20");Q8=makeQuery(id+"F6.opChamfer","BLEND_EDGE",EDGE,{"blendedFrom":[makeQuery(id+"F3.opExtrude","CAP_EDGE",EDGE,{"disambiguationData":[OSD([subQ0])],"isStart":false}),makeQuery(id+"F3.opExtrude","CAP_FACE",FACE,{"disambiguationData":[OSD([sQuery(id+"F2.wireOp",EDGE,"E15"),sQuery(id+"F2.wireOp",EDGE,"E16"),sQuery(id+"F2.wireOp",EDGE,"E17"),sQuery(id+"F2.wireOp",EDGE,"E18"),sQuery(id+"F2.wireOp",EDGE,"E19"),subQ0])],"isStart":false})],"blendedInto":[makeQuery(id+"F3.opExtrude","CAP_FACE",FACE,{"disambiguationData":[OSD([sQuery(id+"F2.wireOp",EDGE,"E15"),sQuery(id+"F2.wireOp",EDGE,"E16"),sQuery(id+"F2.wireOp",EDGE,"E17"),sQuery(id+"F2.wireOp",EDGE,"E18"),sQuery(id+"F2.wireOp",EDGE,"E19"),subQ0])],"isStart":false})]});}
            var Q9;
            {var subQ0=sQuery(id+"F2.wireOp",EDGE,"E15");Q9=makeQuery(id+"F6.opChamfer","BLEND_EDGE",EDGE,{"blendedFrom":[makeQuery(id+"F3.opExtrude","CAP_EDGE",EDGE,{"disambiguationData":[OSD([subQ0])],"isStart":false}),makeQuery(id+"F3.opExtrude","CAP_FACE",FACE,{"disambiguationData":[OSD([subQ0,sQuery(id+"F2.wireOp",EDGE,"E16"),sQuery(id+"F2.wireOp",EDGE,"E17"),sQuery(id+"F2.wireOp",EDGE,"E18"),sQuery(id+"F2.wireOp",EDGE,"E19"),sQuery(id+"F2.wireOp",EDGE,"E20")])],"isStart":false})],"blendedInto":[makeQuery(id+"F3.opExtrude","CAP_FACE",FACE,{"disambiguationData":[OSD([subQ0,sQuery(id+"F2.wireOp",EDGE,"E16"),sQuery(id+"F2.wireOp",EDGE,"E17"),sQuery(id+"F2.wireOp",EDGE,"E18"),sQuery(id+"F2.wireOp",EDGE,"E19"),sQuery(id+"F2.wireOp",EDGE,"E20")])],"isStart":false})]});}
            var Q10;
            Q10=makeQuery(id+"F6.opChamfer","BLEND_EDGE",EDGE,{"blendedFrom":[makeQuery(id+"F3.opExtrude","CAP_EDGE",EDGE,{"disambiguationData":[OSD([sQuery(id+"F2.wireOp",EDGE,"E15")])],"isStart":false}),makeQuery(id+"F3.opExtrude","CAP_EDGE",EDGE,{"disambiguationData":[OSD([sQuery(id+"F2.wireOp",EDGE,"E16")])],"isStart":false})],"blendedInto":[]});
            var Q11;
            Q11=makeQuery(id+"F6.opChamfer","BLEND_EDGE",EDGE,{"blendedFrom":[makeQuery(id+"F3.opExtrude","CAP_EDGE",EDGE,{"disambiguationData":[OSD([sQuery(id+"F2.wireOp",EDGE,"E15")])],"isStart":false}),makeQuery(id+"F3.opExtrude","CAP_EDGE",EDGE,{"disambiguationData":[OSD([sQuery(id+"F2.wireOp",EDGE,"E20")])],"isStart":false})],"blendedInto":[]});
            var Q12;
            Q12=makeQuery(id+"F6.opChamfer","BLEND_EDGE",EDGE,{"blendedFrom":[makeQuery(id+"F5.opExtrude","CAP_EDGE",EDGE,{"disambiguationData":[OSD([sQuery(id+"F4.wireOp",EDGE,"E23")])],"isStart":false}),makeQuery(id+"F5.opExtrude","CAP_EDGE",EDGE,{"disambiguationData":[OSD([sQuery(id+"F4.wireOp",EDGE,"E24")])],"isStart":false})],"blendedInto":[]});
            var Q13;
            {var subQ0=sQuery(id+"F4.wireOp",EDGE,"E24");Q13=makeQuery(id+"F6.opChamfer","BLEND_EDGE",EDGE,{"blendedFrom":[makeQuery(id+"F5.opExtrude","CAP_EDGE",EDGE,{"disambiguationData":[OSD([subQ0])],"isStart":false}),makeQuery(id+"F5.opExtrude","CAP_FACE",FACE,{"disambiguationData":[OSD([sQuery(id+"F4.wireOp",EDGE,"E21"),sQuery(id+"F4.wireOp",EDGE,"E22"),sQuery(id+"F4.wireOp",EDGE,"E23"),subQ0,sQuery(id+"F4.wireOp",EDGE,"E25"),sQuery(id+"F4.wireOp",EDGE,"E26")])],"isStart":false})],"blendedInto":[makeQuery(id+"F5.opExtrude","CAP_FACE",FACE,{"disambiguationData":[OSD([sQuery(id+"F4.wireOp",EDGE,"E21"),sQuery(id+"F4.wireOp",EDGE,"E22"),sQuery(id+"F4.wireOp",EDGE,"E23"),subQ0,sQuery(id+"F4.wireOp",EDGE,"E25"),sQuery(id+"F4.wireOp",EDGE,"E26")])],"isStart":false})]});}
            var Q14;
            {var subQ0=sQuery(id+"F4.wireOp",EDGE,"E25");Q14=makeQuery(id+"F6.opChamfer","BLEND_EDGE",EDGE,{"blendedFrom":[makeQuery(id+"F5.opExtrude","CAP_EDGE",EDGE,{"disambiguationData":[OSD([subQ0])],"isStart":false}),makeQuery(id+"F5.opExtrude","CAP_FACE",FACE,{"disambiguationData":[OSD([sQuery(id+"F4.wireOp",EDGE,"E21"),sQuery(id+"F4.wireOp",EDGE,"E22"),sQuery(id+"F4.wireOp",EDGE,"E23"),sQuery(id+"F4.wireOp",EDGE,"E24"),subQ0,sQuery(id+"F4.wireOp",EDGE,"E26")])],"isStart":false})],"blendedInto":[makeQuery(id+"F5.opExtrude","CAP_FACE",FACE,{"disambiguationData":[OSD([sQuery(id+"F4.wireOp",EDGE,"E21"),sQuery(id+"F4.wireOp",EDGE,"E22"),sQuery(id+"F4.wireOp",EDGE,"E23"),sQuery(id+"F4.wireOp",EDGE,"E24"),subQ0,sQuery(id+"F4.wireOp",EDGE,"E26")])],"isStart":false})]});}
            var Q15;
            Q15=makeQuery(id+"F6.opChamfer","BLEND_EDGE",EDGE,{"blendedFrom":[makeQuery(id+"F5.opExtrude","CAP_EDGE",EDGE,{"disambiguationData":[OSD([sQuery(id+"F4.wireOp",EDGE,"E25")])],"isStart":false}),makeQuery(id+"F5.opExtrude","CAP_EDGE",EDGE,{"disambiguationData":[OSD([sQuery(id+"F4.wireOp",EDGE,"E26")])],"isStart":false})],"blendedInto":[]});
            var Q16;
            Q16=makeQuery(id+"F5.opExtrude","CAP_FACE",FACE,{"disambiguationData":[OSD([sQuery(id+"F4.wireOp",EDGE,"E21"),sQuery(id+"F4.wireOp",EDGE,"E22"),sQuery(id+"F4.wireOp",EDGE,"E23"),sQuery(id+"F4.wireOp",EDGE,"E24"),sQuery(id+"F4.wireOp",EDGE,"E25"),sQuery(id+"F4.wireOp",EDGE,"E26")])],"isStart":false});
            var Q17;
            Q17=makeQuery(id+"F6.opChamfer","BLEND_EDGE",EDGE,{"blendedFrom":[makeQuery(id+"F5.opExtrude","CAP_EDGE",EDGE,{"disambiguationData":[OSD([sQuery(id+"F4.wireOp",EDGE,"E22")])],"isStart":false}),makeQuery(id+"F5.opExtrude","CAP_EDGE",EDGE,{"disambiguationData":[OSD([sQuery(id+"F4.wireOp",EDGE,"E23")])],"isStart":false})],"blendedInto":[]});
            var Q18;
            Q18=makeQuery(id+"F6.opChamfer","BLEND_EDGE",EDGE,{"blendedFrom":[makeQuery(id+"F5.opExtrude","CAP_EDGE",EDGE,{"disambiguationData":[OSD([sQuery(id+"F4.wireOp",EDGE,"E21")])],"isStart":false}),makeQuery(id+"F5.opExtrude","CAP_EDGE",EDGE,{"disambiguationData":[OSD([sQuery(id+"F4.wireOp",EDGE,"E22")])],"isStart":false})],"blendedInto":[]});
            var Q19;
            Q19=makeQuery(id+"F6.opChamfer","BLEND_EDGE",EDGE,{"blendedFrom":[makeQuery(id+"F5.opExtrude","CAP_EDGE",EDGE,{"disambiguationData":[OSD([sQuery(id+"F4.wireOp",EDGE,"E21")])],"isStart":false}),makeQuery(id+"F5.opExtrude","CAP_EDGE",EDGE,{"disambiguationData":[OSD([sQuery(id+"F4.wireOp",EDGE,"E26")])],"isStart":false})],"blendedInto":[]});
            fillet(context, id + "F9", {"entities" : qUnion([Q0, Q1, Q2, Q3, Q4, Q5, Q6, Q7, Q8, Q9, Q10, Q11, Q12, Q13, Q14, Q15, Q16, Q17, Q18, Q19]), "radius" : 50.8 * mm, "tangentPropagation" : true, "allowEdgeOverflow" : false});
        }
    });
